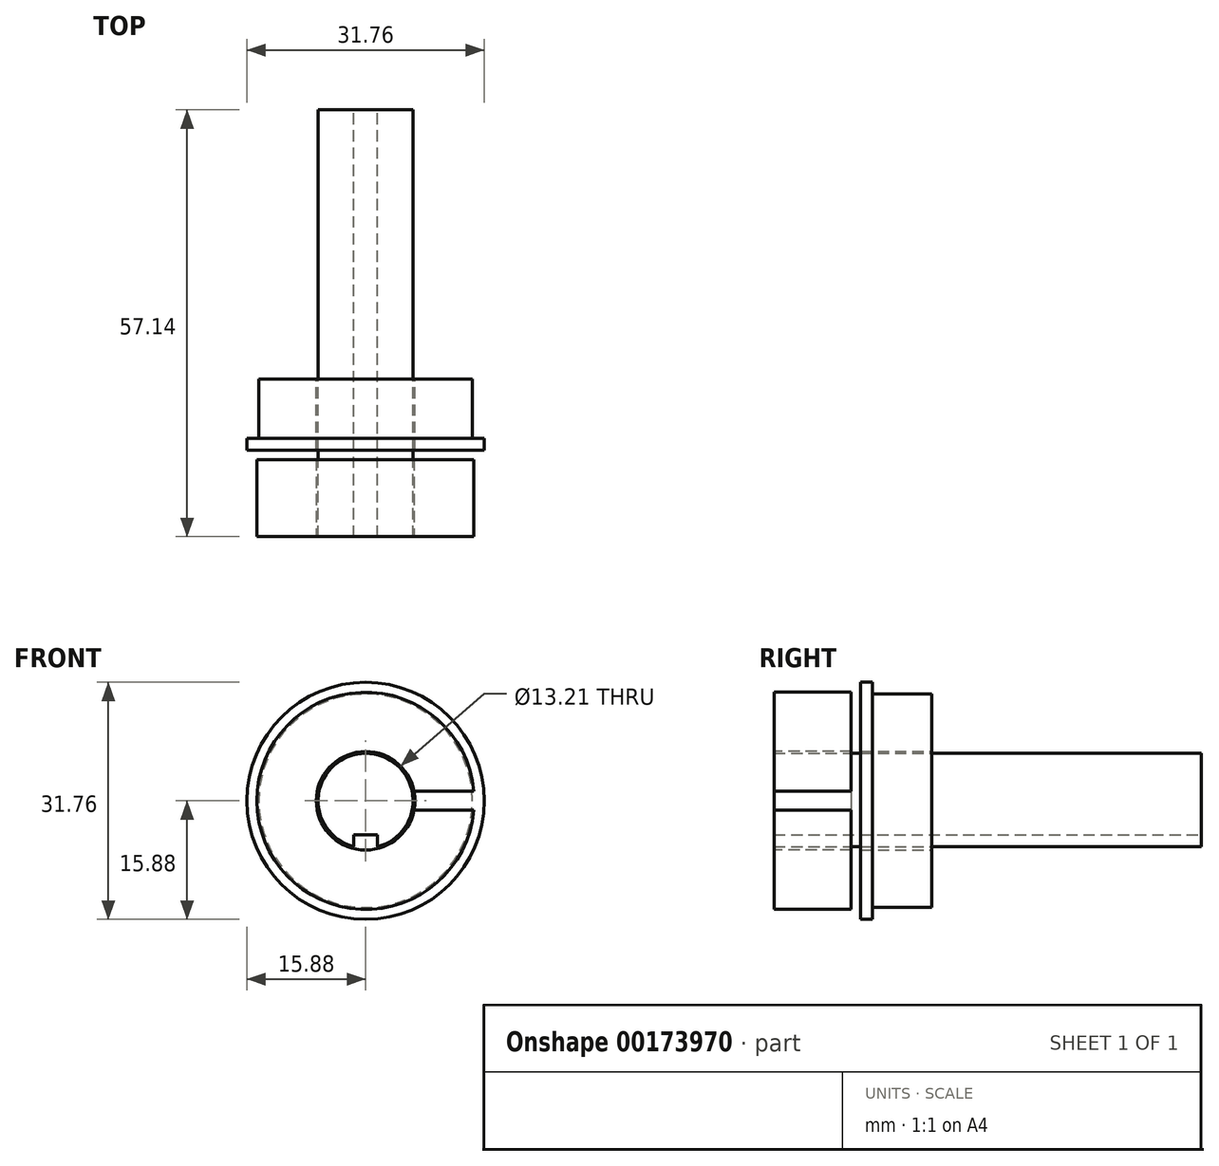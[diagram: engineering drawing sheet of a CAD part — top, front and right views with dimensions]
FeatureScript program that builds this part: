
annotation { "Feature Type Name" : "Feature", "Feature Type Description" : "" }
export const myFeature = defineFeature(function(context is Context, id is Id, definition is map)
    precondition{}
    {
        {
            var Q0;
            Q0=qCreatedBy(makeId("Front.planeOp"),FACE);
            var sketch = newSketch(context, id + "F0", { "sketchPlane" : qUnion([Q0])});
            skArc(sketch, "E0", {"start": v(1.59, -6.15) * mm, "mid": v(0, 6.35) * mm, "end": v(-1.59, -6.15) * mm});
            skLineSegment(sketch, "E1", {"start": v(-1.59, -6.15) * mm, "end": v(-1.59, -4.56) * mm});
            skLineSegment(sketch, "E2", {"start": v(-1.59, -4.56) * mm, "end": v(0, -4.56) * mm});
            skLineSegment(sketch, "E3", {"start": v(0, -4.56) * mm, "end": v(0, 0) * mm, "construction": true});
            skLineSegment(sketch, "E4.MirrorCS", {"start": v(1.59, -4.56) * mm, "end": v(0, -4.56) * mm});
            skLineSegment(sketch, "E5.MirrorCS", {"start": v(1.59, -6.15) * mm, "end": v(1.59, -4.56) * mm});
            skSolve(sketch);
        }
        {
            var Q0;
            Q0=makeQuery(id+"F0.imprint","IMPRINT",FACE,{"disambiguationData":[TD([[makeQuery(id+"F0.imprint","IMPRINT",EDGE,{"derivedFrom":sQuery(id+"F0.wireOp",EDGE,"E0")}),1.0]])]});
            extrude(context, id + "F1", {"entities" : qUnion([Q0]), "endBound" : BoundingType.SYMMETRIC, "depth" : 57.15 * mm});
        }
        {
            var Q0;
            Q0=makeQuery(id+"F1.opExtrude","CAP_FACE",FACE,{"disambiguationData":[OSD([sQuery(id+"F0.wireOp",EDGE,"E0"),sQuery(id+"F0.wireOp",EDGE,"E1"),sQuery(id+"F0.wireOp",EDGE,"E2"),sQuery(id+"F0.wireOp",EDGE,"E4.MirrorCS"),sQuery(id+"F0.wireOp",EDGE,"E5.MirrorCS")])],"isStart":false});
            var sketch = newSketch(context, id + "F2", { "sketchPlane" : qUnion([Q0])});
            skArc(sketch, "E6", {"start": v(6.48, 1.27) * mm, "mid": v(-6.6, 0) * mm, "end": v(6.48, -1.27) * mm});
            skArc(sketch, "E7", {"start": v(14.49, 1.27) * mm, "mid": v(-14.54, 0) * mm, "end": v(14.49, -1.27) * mm});
            skLineSegment(sketch, "E8", {"start": v(0, 0) * mm, "end": v(14.54, 0) * mm, "construction": true});
            skLineSegment(sketch, "E9", {"start": v(6.48, -1.27) * mm, "end": v(14.49, -1.27) * mm});
            skLineSegment(sketch, "E10.MirrorCS", {"start": v(6.48, 1.27) * mm, "end": v(14.49, 1.27) * mm});
            skSolve(sketch);
        }
        {
            var Q0;
            Q0 = qSketchRegion(id + "F2", true);
            extrude(context, id + "F3", {"entities" : qUnion([Q0]), "oppositeDirection" : true, "depth" : 10.32 * mm});
        }
        {
            var Q0;
            Q0=qCreatedBy(makeId("Right.planeOp"),FACE);
            var sketch = newSketch(context, id + "F4", { "sketchPlane" : qUnion([Q0])});
            skLineSegment(sketch, "E11", {"start": v(-16.99, 6.6) * mm, "end": v(-7.46, 6.6) * mm});
            skLineSegment(sketch, "E12", {"start": v(-28.58, 6.35) * mm, "end": v(28.58, 6.35) * mm, "construction": true});
            skLineSegment(sketch, "E13", {"start": v(0, 0) * mm, "end": v(-28.58, 0) * mm, "construction": true});
            skLineSegment(sketch, "E14", {"start": v(-28.58, 0) * mm, "end": v(-28.58, 6.35) * mm, "construction": true});
            skLineSegment(sketch, "E15", {"start": v(-16.99, 6.6) * mm, "end": v(-16.99, 15.88) * mm});
            skLineSegment(sketch, "E16", {"start": v(-16.99, 15.88) * mm, "end": v(-15.4, 15.88) * mm});
            skLineSegment(sketch, "E17", {"start": v(-15.4, 15.88) * mm, "end": v(-15.4, 14.29) * mm});
            skLineSegment(sketch, "E18", {"start": v(-15.4, 14.29) * mm, "end": v(-7.46, 14.29) * mm});
            skLineSegment(sketch, "E19", {"start": v(-7.46, 14.29) * mm, "end": v(-7.46, 6.6) * mm});
            skSolve(sketch);
        }
        {
            var Q0;
            Q0=makeQuery(id+"F4.imprint","IMPRINT",FACE,{"disambiguationData":[TD([[makeQuery(id+"F4.imprint","IMPRINT",EDGE,{"derivedFrom":sQuery(id+"F4.wireOp",EDGE,"E11")}),1.0]])]});
            var Q1;
            Q1=sQuery(id+"F4.wireOp",EDGE,"E13");
            revolve(context, id + "F5", {"entities" : qUnion([Q0]), "axis" : qUnion([Q1]), "revolveType" : RevolveType.FULL});
        }
    });
